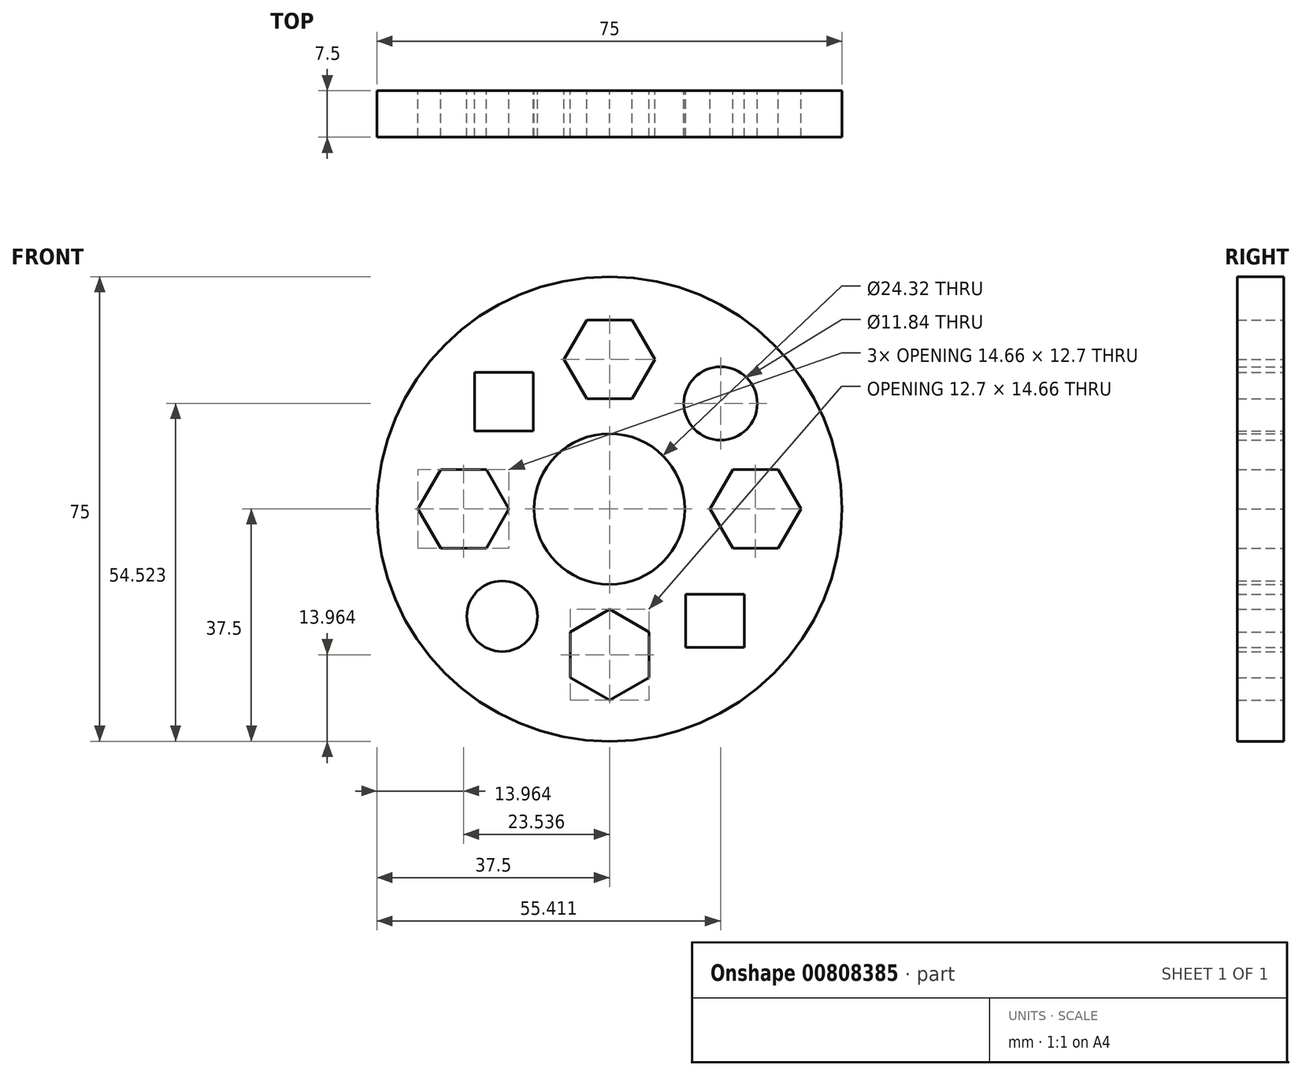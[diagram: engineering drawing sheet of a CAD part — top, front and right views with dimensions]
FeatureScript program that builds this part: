
annotation { "Feature Type Name" : "Feature", "Feature Type Description" : "" }
export const myFeature = defineFeature(function(context is Context, id is Id, definition is map)
    precondition{}
    {
        {
            var Q0;
            Q0=qCreatedBy(makeId("Front.planeOp"),FACE);
            var sketch = newSketch(context, id + "F0", { "sketchPlane" : qUnion([Q0])});
            skCircle(sketch, "E0", {"center": v(0, 0) * mm, "radius": 37.5 * mm});
            skCircle(sketch, "E1", {"center": v(0, 0) * mm, "radius": 12.16 * mm});
            skCircle(sketch, "E2.cCircle", {"center": v(23.54, 0) * mm, "radius": 6.35 * mm, "construction": true});
            skLineSegment(sketch, "E2.0", {"start": v(27.2, -6.35) * mm, "end": v(19.87, -6.35) * mm});
            skLineSegment(sketch, "E2.1", {"start": v(19.87, -6.35) * mm, "end": v(16.2, 0) * mm});
            skLineSegment(sketch, "E2.2", {"start": v(16.2, 0) * mm, "end": v(19.87, 6.35) * mm});
            skLineSegment(sketch, "E2.3", {"start": v(19.87, 6.35) * mm, "end": v(27.2, 6.35) * mm});
            skLineSegment(sketch, "E2.4", {"start": v(27.2, 6.35) * mm, "end": v(30.87, 0) * mm});
            skLineSegment(sketch, "E2.5", {"start": v(30.87, 0) * mm, "end": v(27.2, -6.35) * mm});
            skPoint(sketch, "E2.0.midPoint", {"position": v(23.54, -6.35) * mm});
            skLineSegment(sketch, "E3.1.0", {"start": v(6.35, -27.2) * mm, "end": v(0, -30.87) * mm});
            skCircle(sketch, "E3.1.1", {"center": v(0, -23.54) * mm, "radius": 6.35 * mm, "construction": true});
            skLineSegment(sketch, "E3.1.2", {"start": v(-6.35, -27.2) * mm, "end": v(-6.35, -19.87) * mm});
            skLineSegment(sketch, "E3.1.4", {"start": v(0, -30.87) * mm, "end": v(-6.35, -27.2) * mm});
            skPoint(sketch, "E3.1.5", {"position": v(-6.35, -23.54) * mm});
            skLineSegment(sketch, "E3.1.6", {"start": v(-6.35, -19.87) * mm, "end": v(0, -16.2) * mm});
            skLineSegment(sketch, "E3.1.7", {"start": v(0, -16.2) * mm, "end": v(6.35, -19.87) * mm});
            skLineSegment(sketch, "E3.1.8", {"start": v(6.35, -19.87) * mm, "end": v(6.35, -27.2) * mm});
            skLineSegment(sketch, "E3.2.0", {"start": v(-27.2, -6.35) * mm, "end": v(-30.87, 0) * mm});
            skCircle(sketch, "E3.2.1", {"center": v(-23.54, 0) * mm, "radius": 6.35 * mm, "construction": true});
            skLineSegment(sketch, "E3.2.2", {"start": v(-27.2, 6.35) * mm, "end": v(-19.87, 6.35) * mm});
            skLineSegment(sketch, "E3.2.4", {"start": v(-30.87, 0) * mm, "end": v(-27.2, 6.35) * mm});
            skPoint(sketch, "E3.2.5", {"position": v(-23.54, 6.35) * mm});
            skLineSegment(sketch, "E3.2.6", {"start": v(-19.87, 6.35) * mm, "end": v(-16.2, 0) * mm});
            skLineSegment(sketch, "E3.2.7", {"start": v(-16.2, 0) * mm, "end": v(-19.87, -6.35) * mm});
            skLineSegment(sketch, "E3.2.8", {"start": v(-19.87, -6.35) * mm, "end": v(-27.2, -6.35) * mm});
            skLineSegment(sketch, "E3.anchor1", {"start": v(0, 0) * mm, "end": v(19.87, -6.35) * mm, "construction": true});
            skLineSegment(sketch, "E3.anchor2", {"start": v(0, 0) * mm, "end": v(-19.87, 6.35) * mm, "construction": true});
            skCircle(sketch, "E4.cCircle", {"center": v(0, 24.13) * mm, "radius": 6.35 * mm, "construction": true});
            skLineSegment(sketch, "E4.0", {"start": v(3.67, 17.78) * mm, "end": v(-3.67, 17.78) * mm});
            skLineSegment(sketch, "E4.1", {"start": v(-3.67, 17.78) * mm, "end": v(-7.33, 24.13) * mm});
            skLineSegment(sketch, "E4.2", {"start": v(-7.33, 24.13) * mm, "end": v(-3.67, 30.48) * mm});
            skLineSegment(sketch, "E4.3", {"start": v(-3.67, 30.48) * mm, "end": v(3.67, 30.48) * mm});
            skLineSegment(sketch, "E4.4", {"start": v(3.67, 30.48) * mm, "end": v(7.33, 24.13) * mm});
            skLineSegment(sketch, "E4.5", {"start": v(7.33, 24.13) * mm, "end": v(3.67, 17.78) * mm});
            skPoint(sketch, "E4.0.midPoint", {"position": v(0, 17.78) * mm});
            skLineSegment(sketch, "E5", {"start": v(-19.98, 22.35) * mm, "end": v(-12.88, 14.36) * mm});
            skLineSegment(sketch, "E6", {"start": v(-13.17, 20.87) * mm, "end": v(-20.1, 14.71) * mm});
            skLineSegment(sketch, "E7", {"start": v(13.77, -15.84) * mm, "end": v(22.35, -23.54) * mm});
            skLineSegment(sketch, "E8", {"start": v(14.36, -24.13) * mm, "end": v(22.65, -15.54) * mm});
            skLineSegment(sketch, "E9", {"start": v(20.84, 22.65) * mm, "end": v(15.4, 16.57) * mm});
            skLineSegment(sketch, "E10", {"start": v(15.4, 16.57) * mm, "end": v(20.84, 22.65) * mm});
            skLineSegment(sketch, "E11", {"start": v(20.84, 16.57) * mm, "end": v(14.06, 22.65) * mm});
            skLineSegment(sketch, "E12", {"start": v(-16.13, -16.43) * mm, "end": v(-21.66, -22.59) * mm});
            skLineSegment(sketch, "E13", {"start": v(-15.84, -22.94) * mm, "end": v(-23.9, -15.72) * mm});
            skSolve(sketch);
        }
        {
            var Q0;
            Q0=makeQuery(id+"F0.imprint","IMPRINT",FACE,{"disambiguationData":[TD([[makeQuery(id+"F0.imprint","IMPRINT",EDGE,{"derivedFrom":sQuery(id+"F0.wireOp",EDGE,"E1")}),-1.0]])]});
            extrude(context, id + "F1", {"entities" : qUnion([Q0]), "depth" : 7.5 * mm, "offsetDistance" : 25 * mm, "symmetric" : true});
        }
        {
            var Q0;
            Q0=qCreatedBy(makeId("Front.planeOp"),FACE);
            var sketch = newSketch(context, id + "F2", { "sketchPlane" : qUnion([Q0])});
            skLineSegment(sketch, "E14.bottom", {"start": v(-21.76, 22.06) * mm, "end": v(-12.29, 22.06) * mm});
            skLineSegment(sketch, "E14.top", {"start": v(-21.76, 12.58) * mm, "end": v(-12.29, 12.58) * mm});
            skLineSegment(sketch, "E14.left", {"start": v(-21.76, 22.06) * mm, "end": v(-21.76, 12.58) * mm});
            skLineSegment(sketch, "E14.right", {"start": v(-12.29, 22.06) * mm, "end": v(-12.29, 12.58) * mm});
            skLineSegment(sketch, "E15.bottom", {"start": v(12.29, -13.77) * mm, "end": v(21.76, -13.77) * mm});
            skLineSegment(sketch, "E15.top", {"start": v(12.29, -22.35) * mm, "end": v(21.76, -22.35) * mm});
            skLineSegment(sketch, "E15.left", {"start": v(12.29, -13.77) * mm, "end": v(12.29, -22.35) * mm});
            skLineSegment(sketch, "E15.right", {"start": v(21.76, -13.77) * mm, "end": v(21.76, -22.35) * mm});
            skCircle(sketch, "E16", {"center": v(-17.32, -17.32) * mm, "radius": 5.7 * mm});
            skCircle(sketch, "E17", {"center": v(17.91, 17.02) * mm, "radius": 5.92 * mm});
            skSolve(sketch);
        }
        {
            var Q0;
            Q0 = qSketchRegion(id + "F2", true);
            extrude(context, id + "F3", {"entities" : qUnion([Q0]), "operationType" : NewBodyOperationType.REMOVE, "depth" : 50 * mm, "offsetDistance" : 25 * mm, "symmetric" : true});
        }
    });
